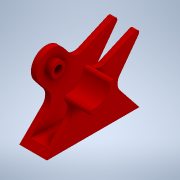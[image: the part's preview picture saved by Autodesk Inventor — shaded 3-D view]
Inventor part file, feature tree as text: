
AUTODESK INVENTOR PART (.ipt)
format: ipt  version: 2020 (Build 240168000, 168)  size: 303,104 bytes
history: native  units: mm
features: extrude x7, sketch x5, projected_geometry x3, mirror x2, plane x1, fillet x1
ambient origin geometry x8: Origin, YZ Plane, XZ Plane, XY Plane, X Axis, Y Axis, Z Axis, Center Point
bodies: Solid1 (feature_tree)
feature tree (19):
  extrude  "Extrusion1"  Depth=27.0mm
  extrude  "Extrusion2"  Depth=5.0mm TaperAngle=0.0deg
  extrude  "Extrusion3"  TaperAngle=0.0deg  [1 undecoded]
  plane  "Work Plane1"
  mirror  "Mirror1"
  extrude  "Extrusion4"  Depth=24.45mm
  sketch  "Sketch5"  dims[d10=52.45mm d12=24.45mm]
  extrude  "Extrusion5"  Depth=10.0mm
  extrude  "Extrusion6"  Depth=6.0mm
  extrude  "Extrusion7"  TaperAngle=0.0deg  [1 undecoded]
  mirror  "Mirror2"
  fillet  "Fillet1"  Radius=7.5mm
  sketch  "Sketch2"  dims[d0=45.0deg d1=27.0mm]
  projected_geometry  "Projected Loop1"
  sketch  "Sketch3"  dims[d2=5.0mm d5=5.0mm d6=0.0mm]
  projected_geometry  "Projected Loop2"
  sketch  "Sketch4"  dims[d8=15.0mm d9=0.0mm]
  projected_geometry  "Projected Loop3"
  sketch  "Sketch6"  dims[d14=7.3mm d15=13.0mm d16=6.0mm d17=0.0mm d18=7.5mm d19=27.8mm d20=0.0mm d21=0.0mm d22=13.9mm d23=5.0mm d24=5.0mm d25=0.0mm d26=19.5mm d27=0.0mm d29=15.0mm d30=0.0mm d31=5.0mm d32=30.0deg d33=35.0mm d34=27.8mm d37=10.0mm d38=8.963942mm]
note: 2 required parameter values undecoded (feature->parameter linkage not recoverable at this tier; creation-order binding heuristic only, values carry confidence <= 0.55)
